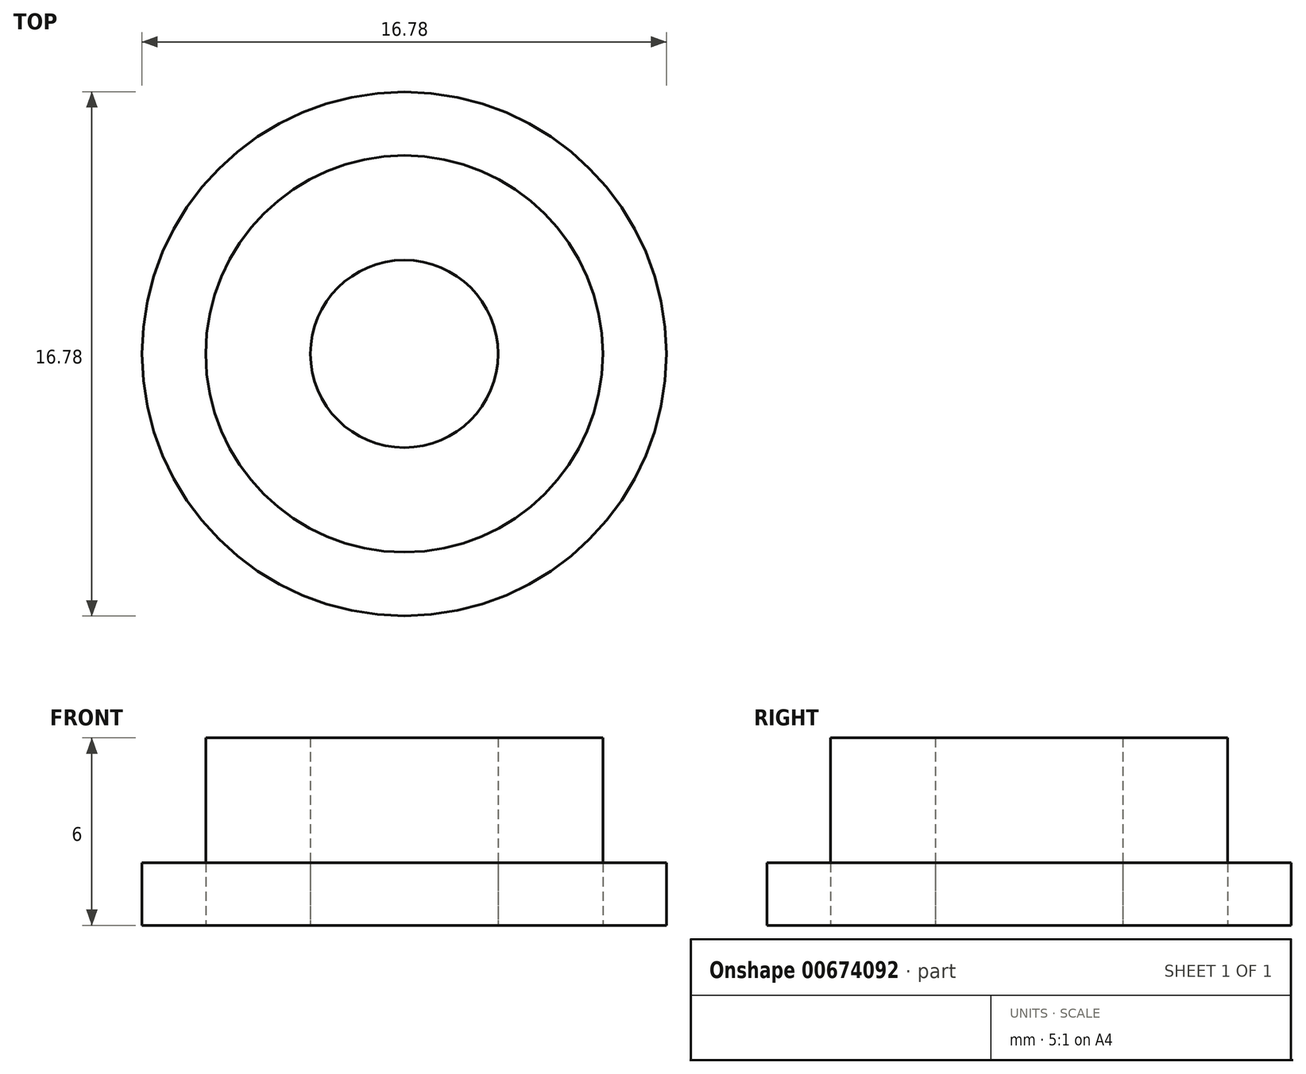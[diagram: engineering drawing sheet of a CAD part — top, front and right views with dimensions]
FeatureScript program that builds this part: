
annotation { "Feature Type Name" : "Feature", "Feature Type Description" : "" }
export const myFeature = defineFeature(function(context is Context, id is Id, definition is map)
    precondition{}
    {
        {
            var Q0;
            Q0=qCreatedBy(makeId("Top.planeOp"),FACE);
            var sketch = newSketch(context, id + "F0", { "sketchPlane" : qUnion([Q0])});
            skCircle(sketch, "E0", {"center": v(0, 0) * mm, "radius": 8.38 * mm});
            skCircle(sketch, "E1", {"center": v(0, 0) * mm, "radius": 6.35 * mm});
            skCircle(sketch, "E2", {"center": v(0, 0) * mm, "radius": 3 * mm});
            skSolve(sketch);
        }
        {
            var Q0;
            Q0=makeQuery(id+"F0.imprint","IMPRINT",FACE,{"disambiguationData":[TD([[makeQuery(id+"F0.imprint","IMPRINT",EDGE,{"derivedFrom":sQuery(id+"F0.wireOp",EDGE,"E0")}),1.0]])]});
            var Q1;
            Q1=makeQuery(id+"F0.imprint","IMPRINT",FACE,{"disambiguationData":[TD([[makeQuery(id+"F0.imprint","IMPRINT",EDGE,{"derivedFrom":sQuery(id+"F0.wireOp",EDGE,"E1")}),1.0]])]});
            extrude(context, id + "F1", {"entities" : qUnion([Q0, Q1]), "depth" : 2 * mm, "offsetDistance" : 25 * mm});
        }
        {
            var Q0;
            Q0=makeQuery(id+"F0.imprint","IMPRINT",FACE,{"disambiguationData":[TD([[makeQuery(id+"F0.imprint","IMPRINT",EDGE,{"derivedFrom":sQuery(id+"F0.wireOp",EDGE,"E1")}),1.0]])]});
            extrude(context, id + "F2", {"entities" : qUnion([Q0]), "depth" : 6 * mm, "offsetDistance" : 25 * mm});
        }
    });
